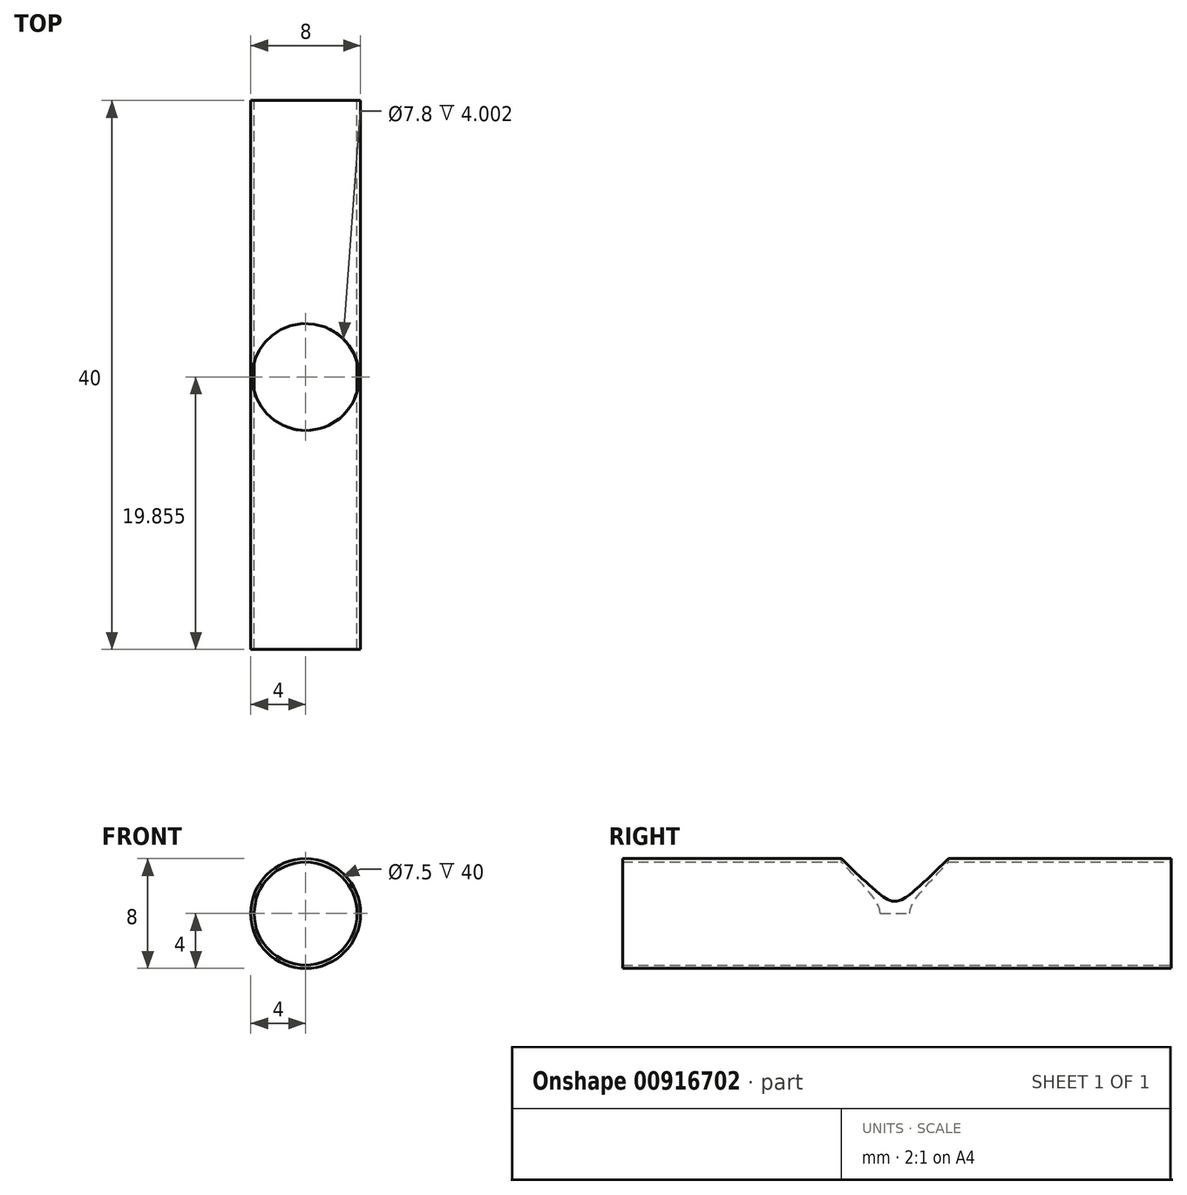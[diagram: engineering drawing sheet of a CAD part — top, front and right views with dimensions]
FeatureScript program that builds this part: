
annotation { "Feature Type Name" : "Feature", "Feature Type Description" : "" }
export const myFeature = defineFeature(function(context is Context, id is Id, definition is map)
    precondition{}
    {
        {
            var Q0;
            Q0=qCreatedBy(makeId("Front.planeOp"),FACE);
            var sketch = newSketch(context, id + "F0", { "sketchPlane" : qUnion([Q0])});
            skCircle(sketch, "E0", {"center": v(0, 0) * mm, "radius": 4 * mm});
            skCircle(sketch, "E1", {"center": v(0, 0) * mm, "radius": 3.75 * mm});
            skSolve(sketch);
        }
        {
            var Q0;
            Q0=qCreatedBy(makeId("Top.planeOp"),FACE);
            var sketch = newSketch(context, id + "F1", { "sketchPlane" : qUnion([Q0])});
            skLineSegment(sketch, "E2", {"start": v(0, 0) * mm, "end": v(0, 40) * mm});
            skSolve(sketch);
        }
        {
            var Q0;
            Q0 = qSketchRegion(id + "F0", true);
            var Q1;
            Q1 = qConstructionFilter(qBodyType(qCreatedBy(id + "F1" ,EDGE), BodyType.WIRE), ConstructionObject.NO);
            sweep(context, id + "F2", {"profiles" : qUnion([Q0]), "path" : qUnion([Q1])});
        }
        {
            var Q0;
            Q0=qCreatedBy(makeId("Top.planeOp"),FACE);
            var sketch = newSketch(context, id + "F3", { "sketchPlane" : qUnion([Q0])});
            skCircle(sketch, "E3", {"center": v(0, 19.86) * mm, "radius": 3.9 * mm});
            skSolve(sketch);
        }
        {
            var Q0;
            Q0=qCreatedBy(makeId("Right.planeOp"),FACE);
            var sketch = newSketch(context, id + "F4", { "sketchPlane" : qUnion([Q0])});
            skLineSegment(sketch, "E4", {"start": v(21.2, 0) * mm, "end": v(21.2, 30) * mm});
            skSolve(sketch);
        }
        {
            var Q0;
            Q0 = qSketchRegion(id + "F3", true);
            var Q1;
            Q1 = qConstructionFilter(qBodyType(qCreatedBy(id + "F4" ,EDGE), BodyType.WIRE), ConstructionObject.NO);
            sweep(context, id + "F5", {"operationType" : NewBodyOperationType.REMOVE, "profiles" : qUnion([Q0]), "path" : qUnion([Q1])});
        }
    });
